# Revit family: Узел герметизации_01.03
name_source: partatom
category: Соединительные детали трубопроводов
units: mm (PartAtom-declared; Revit-internal decimal feet)

## family parameters
Всегда вертикально = Нет
На основе рабочей плоскости = Нет
Общий = Нет
При загрузке вырезать с полостями = Нет
Размер круглого соединителя = Использовать диаметр
Тип детали = Соединение

## types (1)
- Узел герметизации_01.03
    LT = Уплотнители АР
    АР100 = Тип уплотнителя : АР100
    АР200 = Тип уплотнителя : АР200
    АР215 = Тип уплотнителя : АР215
    АР250 = Тип уплотнителя : АР250
    АР265 = Тип уплотнителя : АР265
    АР300 = Тип уплотнителя : АР300
    АР310 = Тип уплотнителя : АР310
    АР315 = Тип уплотнителя : АР315
    АР325 = Тип уплотнителя : АР325
    АР350 = Тип уплотнителя : АР350
    АР365 = Тип уплотнителя : АР365
    АР375 = Тип уплотнителя : АР375
    АР400 = Тип уплотнителя : АР400
    АР415 = Тип уплотнителя : АР415
    АР425 = Тип уплотнителя : АР425
    АР450 = Тип уплотнителя : АР450
    АР465 = Тип уплотнителя : АР465
    АР475 = Тип уплотнителя : АР475
    АР480 = Тип уплотнителя : АР480
    АР500 = Тип уплотнителя : АР500
    АР525 = Тип уплотнителя : АР525
    АР550 = Тип уплотнителя : АР550
    АР565 = Тип уплотнителя : АР565
    АР600 = Тип уплотнителя : АР600
    АР615 = Тип уплотнителя : АР615
    АР650 = Тип уплотнителя : АР650
    АР665 = Тип уплотнителя : АР665
    АР675 = Тип уплотнителя : АР675
    АР800 = Тип уплотнителя : АР800
    АР865 = Тип уплотнителя : АР865
    АС_Количество = 1
    АС_Наименование = Узел герметизации N1
    Материал гидроворотника = <По категории>
    Материал гильзы = <По категории>
    Материал манжеты = <По категории>
    Материал уплотнителей = <По категории>
    Материал хомутов = <По категории>
    Отметка по умолчанию = 0 мм
    Производитель = ООО"АктивПитерСтрой"
    Сайт = https://aktivring.ru
